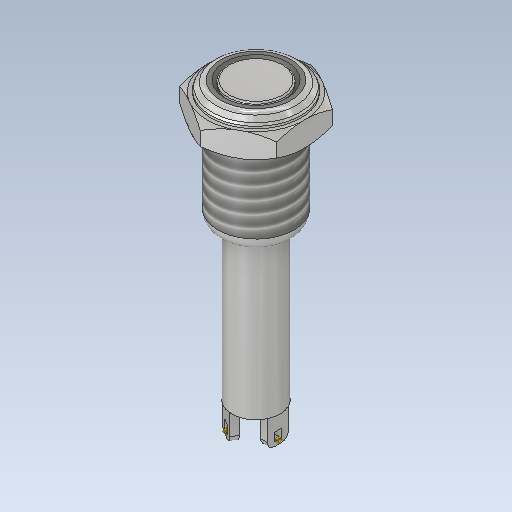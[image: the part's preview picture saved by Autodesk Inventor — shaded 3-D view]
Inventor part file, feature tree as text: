
AUTODESK INVENTOR PART (.ipt)
format: ipt  version: 2020.1 (Build 241239000, 239)  size: 307,712 bytes
history: native  units: mm
features: extrude x9, sketch x6, fillet x4, chamfer x3, revolve x1, boolean_combine x1, plane x1, other x1, pattern_circular x1, thread x1
ambient origin geometry x8: Origin, YZ Plane, XZ Plane, XY Plane, X Axis, Y Axis, Z Axis, Center Point
bodies: Solid1 (feature_tree), Solid2 (feature_tree)
feature tree (28):
  sketch  "Sketch1"  dims[d0=13.0mm d1=14.0mm]
  extrude  "Extrusion1"  Depth=14.0mm
  extrude  "Extrusion2"  Depth=18.0mm TaperAngle=0.0deg
  extrude  "Extrusion3"  Depth=5.0mm TaperAngle=0.0deg
  extrude  "Extrusion4"  Depth=1.0mm TaperAngle=45.0deg
  sketch  "Sketch3"  dims[d5=5.0mm d6=0.0mm d7=5.0mm d8=0.0mm]
  chamfer  "Chamfer1"  Distance=8.0mm
  fillet  "Fillet1"  Radius=1.0mm
  fillet  "Fillet2"  Radius=0.5mm
  sketch  "Sketch2"  dims[d2=11.0mm d3=18.0mm d4=0.0mm]
  extrude  "Extrusion5"  Depth=1.0mm TaperAngle=0.0deg
  chamfer  "Chamfer2"  Distance=0.2mm
  extrude  "Extrusion6"  Depth=3.5mm
  fillet  "Fillet3"  Radius=1.0mm
  revolve  "Revolution1"  [1 undecoded]
  boolean_combine  "Combine1"
  extrude  "Extrusion10"  Depth=2.0mm
  plane  "Work Plane1"
  extrude  "Extrusion7"  TaperAngle=90.0deg  [1 undecoded]
  fillet  "Fillet4"  Radius=1.0mm
  extrude  "Extrusion8"  Depth=2.0mm
  other  "Work Axis1"
  pattern_circular  "Circular Pattern1"  Count=3 Angle=360.0deg
  thread  "Thread1"  [1 undecoded]
  chamfer  "Chamfer3"  Distance=1.0mm
  sketch  "Sketch4"  dims[d9=1.5mm d10=0.0mm d11=1.0mm d12=2.0mm d13=45.0deg]
  sketch  "Sketch5"  dims[d14=1.0mm]
  sketch  "Sketch7"  dims[d15=2.0mm d16=8.0mm d17=1.0mm d18=0.0mm d19=0.5mm d20=2.0mm d21=45.0deg d22=1.0mm d23=0.0mm d24=0.2mm d25=3.5mm d26=1.0mm d27=6.108652mm d28=6.108652mm d29=90.0deg d31=1.0mm d32=3.0mm d33=30.0mm d35=360.0deg d37=1.0mm d38=0.0mm d39=1.0mm d40=1.2mm d41=1.0mm d42=0.0mm d43=30.0mm d44=360.0deg d46=10.0mm d47=0.0mm d48=0.2mm d49=2.0mm d50=45.0deg d53=22.0mm d54=0.0mm d55=4.0mm]
note: 3 required parameter values undecoded (feature->parameter linkage not recoverable at this tier; creation-order binding heuristic only, values carry confidence <= 0.55)